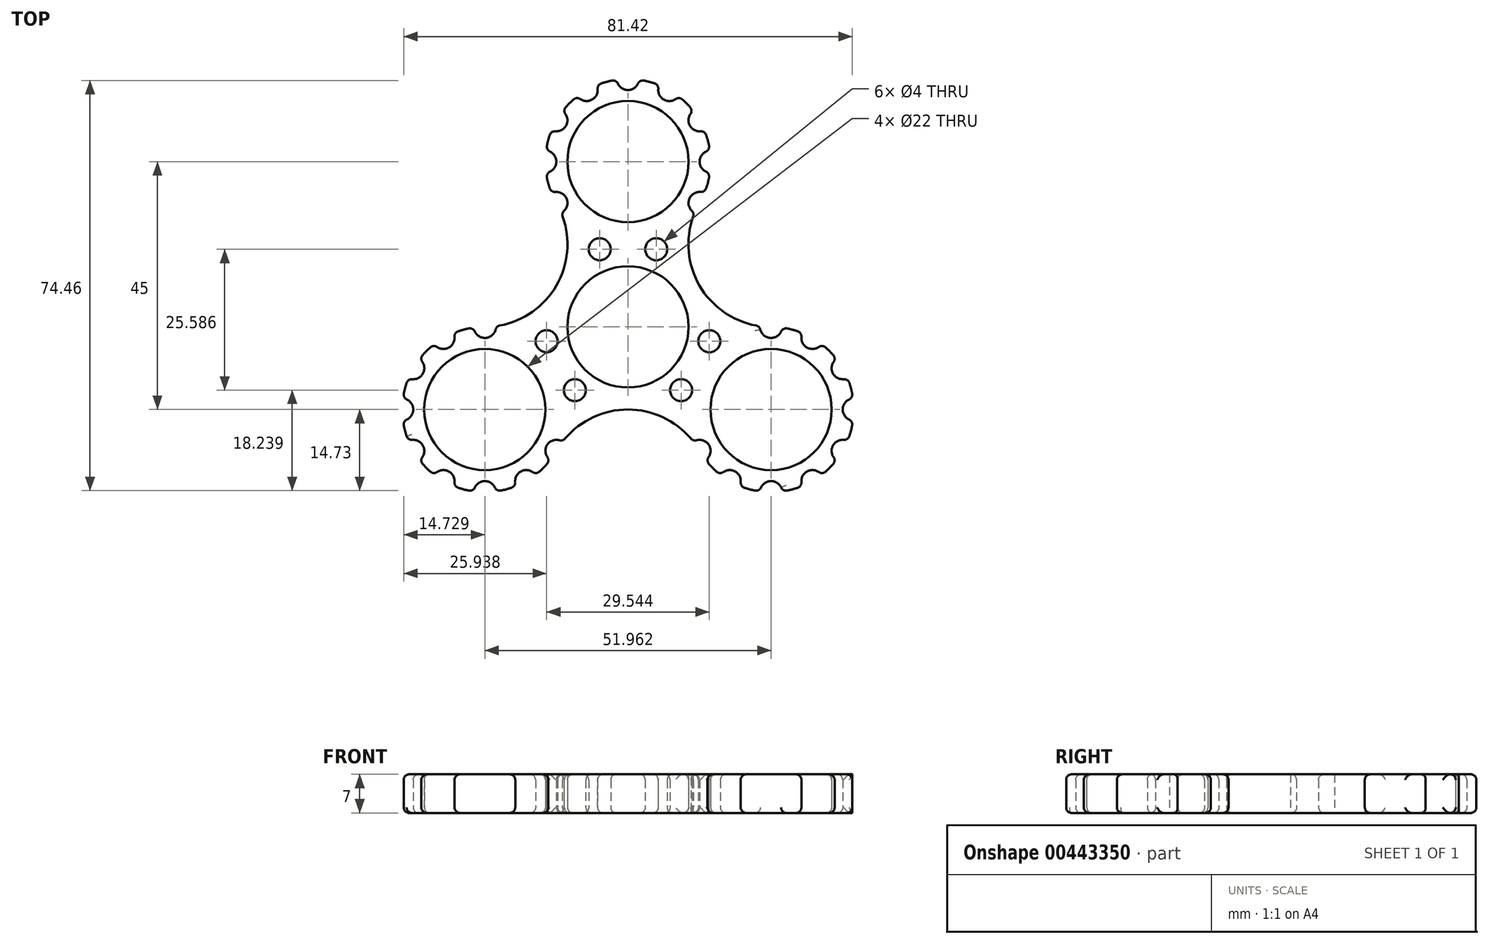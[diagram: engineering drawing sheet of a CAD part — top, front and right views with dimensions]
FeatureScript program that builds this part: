
annotation { "Feature Type Name" : "Feature", "Feature Type Description" : "" }
export const myFeature = defineFeature(function(context is Context, id is Id, definition is map)
    precondition{}
    {
        {
            var Q0;
            Q0=qCreatedBy(makeId("Top.planeOp"),FACE);
            var sketch = newSketch(context, id + "F0", { "sketchPlane" : qUnion([Q0])});
            skCircle(sketch, "E0", {"center": v(0, 0) * mm, "radius": 11 * mm});
            skCircle(sketch, "E1.0", {"center": v(0, 0) * mm, "radius": 14 * mm});
            skCircle(sketch, "E2", {"center": v(0, 30) * mm, "radius": 11 * mm});
            skArc(sketch, "E3.0", {"start": v(13, 22.5) * mm, "mid": v(0, 45) * mm, "end": v(-13, 22.5) * mm});
            skLineSegment(sketch, "E4", {"start": v(0, 14) * mm, "end": v(0, 30) * mm});
            skCircle(sketch, "E5.1.0", {"center": v(-25.98, -15) * mm, "radius": 11 * mm});
            skArc(sketch, "E5.1.1", {"start": v(-25.98, 0) * mm, "mid": v(-38.97, -22.5) * mm, "end": v(-13, -22.5) * mm});
            skCircle(sketch, "E5.2.0", {"center": v(25.98, -15) * mm, "radius": 11 * mm});
            skArc(sketch, "E5.2.1", {"start": v(13, -22.5) * mm, "mid": v(38.97, -22.5) * mm, "end": v(25.98, 0) * mm});
            skArc(sketch, "E6", {"start": v(-13, 22.5) * mm, "mid": v(-13, 7.5) * mm, "end": v(-25.98, 0) * mm});
            skArc(sketch, "E7", {"start": v(25.98, 0) * mm, "mid": v(13, 7.5) * mm, "end": v(13, 22.5) * mm});
            skArc(sketch, "E8", {"start": v(-13, -22.5) * mm, "mid": v(0, -15) * mm, "end": v(13, -22.5) * mm});
            skPoint(sketch, "E9", {"position": v(-13, 7.5) * mm});
            skCircle(sketch, "E10.1.0", {"center": v(-14.77, -2.6) * mm, "radius": 2 * mm});
            skCircle(sketch, "E10.2.0", {"center": v(-9.64, -11.5) * mm, "radius": 2 * mm});
            skCircle(sketch, "E10.4.0", {"center": v(9.64, -11.5) * mm, "radius": 2 * mm});
            skCircle(sketch, "E10.5.0", {"center": v(14.77, -2.6) * mm, "radius": 2 * mm});
            skCircle(sketch, "E10.7.0", {"center": v(5.13, 14.1) * mm, "radius": 2 * mm});
            skCircle(sketch, "E10.8.0", {"center": v(-5.13, 14.1) * mm, "radius": 2 * mm});
            skCircle(sketch, "E11", {"center": v(25.98, 0) * mm, "radius": 2 * mm});
            skCircle(sketch, "E12.1.0", {"center": v(33.48, -2) * mm, "radius": 2 * mm});
            skCircle(sketch, "E12.2.0", {"center": v(38.97, -7.5) * mm, "radius": 2 * mm});
            skCircle(sketch, "E12.3.0", {"center": v(40.98, -15) * mm, "radius": 2 * mm});
            skCircle(sketch, "E12.4.0", {"center": v(38.97, -22.5) * mm, "radius": 2 * mm});
            skCircle(sketch, "E12.5.0", {"center": v(33.48, -28) * mm, "radius": 2 * mm});
            skCircle(sketch, "E12.6.0", {"center": v(25.98, -30) * mm, "radius": 2 * mm});
            skCircle(sketch, "E12.7.0", {"center": v(18.48, -28) * mm, "radius": 2 * mm});
            skCircle(sketch, "E12.8.0", {"center": v(13, -22.5) * mm, "radius": 2 * mm});
            skLineSegment(sketch, "E12.anchor1", {"start": v(25.98, -15) * mm, "end": v(25.98, 0) * mm, "construction": true});
            skLineSegment(sketch, "E12.anchor2", {"start": v(25.98, -15) * mm, "end": v(13, -22.5) * mm, "construction": true});
            skCircle(sketch, "E13.1.0", {"center": v(-13, 22.5) * mm, "radius": 2 * mm});
            skCircle(sketch, "E13.1.1", {"center": v(-15, 30) * mm, "radius": 2 * mm});
            skCircle(sketch, "E13.1.2", {"center": v(-13, 37.5) * mm, "radius": 2 * mm});
            skCircle(sketch, "E13.1.3", {"center": v(-7.5, 43) * mm, "radius": 2 * mm});
            skCircle(sketch, "E13.1.4", {"center": v(0, 45) * mm, "radius": 2 * mm});
            skCircle(sketch, "E13.1.5", {"center": v(7.5, 43) * mm, "radius": 2 * mm});
            skCircle(sketch, "E13.1.6", {"center": v(13, 37.5) * mm, "radius": 2 * mm});
            skCircle(sketch, "E13.1.7", {"center": v(15, 30) * mm, "radius": 2 * mm});
            skCircle(sketch, "E13.1.8", {"center": v(13, 22.5) * mm, "radius": 2 * mm});
            skCircle(sketch, "E13.2.0", {"center": v(-13, -22.5) * mm, "radius": 2 * mm});
            skCircle(sketch, "E13.2.1", {"center": v(-18.48, -28) * mm, "radius": 2 * mm});
            skCircle(sketch, "E13.2.2", {"center": v(-25.98, -30) * mm, "radius": 2 * mm});
            skCircle(sketch, "E13.2.3", {"center": v(-33.48, -28) * mm, "radius": 2 * mm});
            skCircle(sketch, "E13.2.4", {"center": v(-38.97, -22.5) * mm, "radius": 2 * mm});
            skCircle(sketch, "E13.2.5", {"center": v(-40.98, -15) * mm, "radius": 2 * mm});
            skCircle(sketch, "E13.2.6", {"center": v(-38.97, -7.5) * mm, "radius": 2 * mm});
            skCircle(sketch, "E13.2.7", {"center": v(-33.48, -2) * mm, "radius": 2 * mm});
            skCircle(sketch, "E13.2.8", {"center": v(-25.98, 0) * mm, "radius": 2 * mm});
            skSolve(sketch);
        }
        {
            var Q0;
            Q0=makeQuery(id+"F0.imprint","IMPRINT",FACE,{"disambiguationData":[TD([[makeQuery(id+"F0.imprint","IMPRINT",EDGE,{"derivedFrom":sQuery(id+"F0.wireOp",EDGE,"E2")}),-1.0]])]});
            var Q1;
            Q1=makeQuery(id+"F0.imprint","IMPRINT",FACE,{"disambiguationData":[TD([[makeQuery(id+"F0.imprint","IMPRINT",EDGE,{"derivedFrom":sQuery(id+"F0.wireOp",EDGE,"E0")}),-1.0]])]});
            extrude(context, id + "F1", {"entities" : qUnion([Q0, Q1]), "endBound" : BoundingType.SYMMETRIC, "depth" : 7 * mm});
        }
        {
            var Q0;
            {var subQ0=sQuery(id+"F0.wireOp",EDGE,"E5.1.1");Q0=makeQuery(id+"F1.opExtrude","SWEPT_FACE",FACE,{"disambiguationData":[OSD([subQ0]),TDD([makeQuery(id+"F0.imprint","IMPRINT",EDGE,{"disambiguationData":[TD([[makeQuery(id+"F0.imprint","INTERSECT",VERTEX,{"disambiguationData":[OD(1.0)],"derivedFrom":[subQ0,sQuery(id+"F0.wireOp",EDGE,"E13.2.6")]}),-1.0]])],"derivedFrom":subQ0})])]});}
            var Q1;
            Q1=makeQuery(id+"F1.opExtrude","SWEPT_FACE",FACE,{"disambiguationData":[OSD([sQuery(id+"F0.wireOp",EDGE,"E13.2.5")])]});
            var Q2;
            {var subQ0=sQuery(id+"F0.wireOp",EDGE,"E5.1.1");Q2=makeQuery(id+"F1.opExtrude","SWEPT_FACE",FACE,{"disambiguationData":[OSD([subQ0]),TDD([makeQuery(id+"F0.imprint","IMPRINT",EDGE,{"disambiguationData":[TD([[makeQuery(id+"F0.imprint","INTERSECT",VERTEX,{"disambiguationData":[OD(1.0)],"derivedFrom":[subQ0,sQuery(id+"F0.wireOp",EDGE,"E13.2.5")]}),-1.0]])],"derivedFrom":subQ0})])]});}
            var Q3;
            Q3=makeQuery(id+"F1.opExtrude","SWEPT_FACE",FACE,{"disambiguationData":[OSD([sQuery(id+"F0.wireOp",EDGE,"E13.2.4")])]});
            var Q4;
            {var subQ0=sQuery(id+"F0.wireOp",EDGE,"E5.1.1");Q4=makeQuery(id+"F1.opExtrude","SWEPT_FACE",FACE,{"disambiguationData":[OSD([subQ0]),TDD([makeQuery(id+"F0.imprint","IMPRINT",EDGE,{"disambiguationData":[TD([[makeQuery(id+"F0.imprint","INTERSECT",VERTEX,{"disambiguationData":[OD(1.0)],"derivedFrom":[subQ0,sQuery(id+"F0.wireOp",EDGE,"E13.2.4")]}),-1.0]])],"derivedFrom":subQ0})])]});}
            var Q5;
            Q5=makeQuery(id+"F1.opExtrude","SWEPT_FACE",FACE,{"disambiguationData":[OSD([sQuery(id+"F0.wireOp",EDGE,"E13.2.3")])]});
            var Q6;
            {var subQ0=sQuery(id+"F0.wireOp",EDGE,"E5.1.1");Q6=makeQuery(id+"F1.opExtrude","SWEPT_FACE",FACE,{"disambiguationData":[OSD([subQ0]),TDD([makeQuery(id+"F0.imprint","IMPRINT",EDGE,{"disambiguationData":[TD([[makeQuery(id+"F0.imprint","INTERSECT",VERTEX,{"disambiguationData":[OD(1.0)],"derivedFrom":[subQ0,sQuery(id+"F0.wireOp",EDGE,"E13.2.3")]}),-1.0]])],"derivedFrom":subQ0})])]});}
            var Q7;
            Q7=makeQuery(id+"F1.opExtrude","SWEPT_FACE",FACE,{"disambiguationData":[OSD([sQuery(id+"F0.wireOp",EDGE,"E13.2.2")])]});
            var Q8;
            {var subQ0=sQuery(id+"F0.wireOp",EDGE,"E5.1.1");Q8=makeQuery(id+"F1.opExtrude","SWEPT_FACE",FACE,{"disambiguationData":[OSD([subQ0]),TDD([makeQuery(id+"F0.imprint","IMPRINT",EDGE,{"disambiguationData":[TD([[makeQuery(id+"F0.imprint","INTERSECT",VERTEX,{"disambiguationData":[OD(1.0)],"derivedFrom":[subQ0,sQuery(id+"F0.wireOp",EDGE,"E13.2.2")]}),-1.0]])],"derivedFrom":subQ0})])]});}
            var Q9;
            Q9=makeQuery(id+"F1.opExtrude","SWEPT_FACE",FACE,{"disambiguationData":[OSD([sQuery(id+"F0.wireOp",EDGE,"E13.2.6")])]});
            var Q10;
            Q10=makeQuery(id+"F1.opExtrude","SWEPT_FACE",FACE,{"disambiguationData":[OSD([sQuery(id+"F0.wireOp",EDGE,"E13.2.1")])]});
            var Q11;
            {var subQ0=sQuery(id+"F0.wireOp",EDGE,"E5.1.1");Q11=makeQuery(id+"F1.opExtrude","SWEPT_FACE",FACE,{"disambiguationData":[OSD([subQ0]),TDD([makeQuery(id+"F0.imprint","IMPRINT",EDGE,{"disambiguationData":[TD([[makeQuery(id+"F0.imprint","INTERSECT",VERTEX,{"disambiguationData":[OD(1.0)],"derivedFrom":[subQ0,sQuery(id+"F0.wireOp",EDGE,"E13.2.1")]}),-1.0]])],"derivedFrom":subQ0})])]});}
            var Q12;
            Q12=makeQuery(id+"F1.opExtrude","SWEPT_FACE",FACE,{"disambiguationData":[OSD([sQuery(id+"F0.wireOp",EDGE,"E13.2.0")])]});
            var Q13;
            Q13=makeQuery(id+"F1.opExtrude","SWEPT_FACE",FACE,{"disambiguationData":[OSD([sQuery(id+"F0.wireOp",EDGE,"E8")])]});
            var Q14;
            Q14=makeQuery(id+"F1.opExtrude","SWEPT_FACE",FACE,{"disambiguationData":[OSD([sQuery(id+"F0.wireOp",EDGE,"E12.8.0")])]});
            var Q15;
            {var subQ0=sQuery(id+"F0.wireOp",EDGE,"E5.2.1");Q15=makeQuery(id+"F1.opExtrude","SWEPT_FACE",FACE,{"disambiguationData":[OSD([subQ0]),TDD([makeQuery(id+"F0.imprint","IMPRINT",EDGE,{"disambiguationData":[TD([[makeQuery(id+"F0.imprint","INTERSECT",VERTEX,{"derivedFrom":[subQ0,sQuery(id+"F0.wireOp",EDGE,"E12.8.0")]}),-1.0]])],"derivedFrom":subQ0})])]});}
            var Q16;
            Q16=makeQuery(id+"F1.opExtrude","SWEPT_FACE",FACE,{"disambiguationData":[OSD([sQuery(id+"F0.wireOp",EDGE,"E12.7.0")])]});
            var Q17;
            {var subQ0=sQuery(id+"F0.wireOp",EDGE,"E5.2.1");Q17=makeQuery(id+"F1.opExtrude","SWEPT_FACE",FACE,{"disambiguationData":[OSD([subQ0]),TDD([makeQuery(id+"F0.imprint","IMPRINT",EDGE,{"disambiguationData":[TD([[makeQuery(id+"F0.imprint","INTERSECT",VERTEX,{"disambiguationData":[OD(1.0)],"derivedFrom":[subQ0,sQuery(id+"F0.wireOp",EDGE,"E12.7.0")]}),-1.0]])],"derivedFrom":subQ0})])]});}
            var Q18;
            Q18=makeQuery(id+"F1.opExtrude","SWEPT_FACE",FACE,{"disambiguationData":[OSD([sQuery(id+"F0.wireOp",EDGE,"E12.6.0")])]});
            var Q19;
            {var subQ0=sQuery(id+"F0.wireOp",EDGE,"E5.2.1");Q19=makeQuery(id+"F1.opExtrude","SWEPT_FACE",FACE,{"disambiguationData":[OSD([subQ0]),TDD([makeQuery(id+"F0.imprint","IMPRINT",EDGE,{"disambiguationData":[TD([[makeQuery(id+"F0.imprint","INTERSECT",VERTEX,{"disambiguationData":[OD(1.0)],"derivedFrom":[subQ0,sQuery(id+"F0.wireOp",EDGE,"E12.6.0")]}),-1.0]])],"derivedFrom":subQ0})])]});}
            var Q20;
            Q20=makeQuery(id+"F1.opExtrude","SWEPT_FACE",FACE,{"disambiguationData":[OSD([sQuery(id+"F0.wireOp",EDGE,"E12.5.0")])]});
            var Q21;
            {var subQ0=sQuery(id+"F0.wireOp",EDGE,"E5.2.1");Q21=makeQuery(id+"F1.opExtrude","SWEPT_FACE",FACE,{"disambiguationData":[OSD([subQ0]),TDD([makeQuery(id+"F0.imprint","IMPRINT",EDGE,{"disambiguationData":[TD([[makeQuery(id+"F0.imprint","INTERSECT",VERTEX,{"disambiguationData":[OD(1.0)],"derivedFrom":[subQ0,sQuery(id+"F0.wireOp",EDGE,"E12.5.0")]}),-1.0]])],"derivedFrom":subQ0})])]});}
            var Q22;
            Q22=makeQuery(id+"F1.opExtrude","SWEPT_FACE",FACE,{"disambiguationData":[OSD([sQuery(id+"F0.wireOp",EDGE,"E12.4.0")])]});
            var Q23;
            {var subQ0=sQuery(id+"F0.wireOp",EDGE,"E5.2.1");Q23=makeQuery(id+"F1.opExtrude","SWEPT_FACE",FACE,{"disambiguationData":[OSD([subQ0]),TDD([makeQuery(id+"F0.imprint","IMPRINT",EDGE,{"disambiguationData":[TD([[makeQuery(id+"F0.imprint","INTERSECT",VERTEX,{"disambiguationData":[OD(1.0)],"derivedFrom":[subQ0,sQuery(id+"F0.wireOp",EDGE,"E12.4.0")]}),-1.0]])],"derivedFrom":subQ0})])]});}
            var Q24;
            Q24=makeQuery(id+"F1.opExtrude","SWEPT_FACE",FACE,{"disambiguationData":[OSD([sQuery(id+"F0.wireOp",EDGE,"E12.3.0")])]});
            var Q25;
            {var subQ0=sQuery(id+"F0.wireOp",EDGE,"E5.2.1");Q25=makeQuery(id+"F1.opExtrude","SWEPT_FACE",FACE,{"disambiguationData":[OSD([subQ0]),TDD([makeQuery(id+"F0.imprint","IMPRINT",EDGE,{"disambiguationData":[TD([[makeQuery(id+"F0.imprint","INTERSECT",VERTEX,{"disambiguationData":[OD(1.0)],"derivedFrom":[subQ0,sQuery(id+"F0.wireOp",EDGE,"E12.3.0")]}),-1.0]])],"derivedFrom":subQ0})])]});}
            var Q26;
            {var subQ0=sQuery(id+"F0.wireOp",EDGE,"E5.2.1");Q26=makeQuery(id+"F1.opExtrude","SWEPT_FACE",FACE,{"disambiguationData":[OSD([subQ0]),TDD([makeQuery(id+"F0.imprint","IMPRINT",EDGE,{"disambiguationData":[TD([[makeQuery(id+"F0.imprint","INTERSECT",VERTEX,{"disambiguationData":[OD(1.0)],"derivedFrom":[subQ0,sQuery(id+"F0.wireOp",EDGE,"E12.2.0")]}),-1.0]])],"derivedFrom":subQ0})])]});}
            var Q27;
            Q27=makeQuery(id+"F1.opExtrude","SWEPT_FACE",FACE,{"disambiguationData":[OSD([sQuery(id+"F0.wireOp",EDGE,"E12.1.0")])]});
            var Q28;
            Q28=makeQuery(id+"F1.opExtrude","SWEPT_FACE",FACE,{"disambiguationData":[OSD([sQuery(id+"F0.wireOp",EDGE,"E12.2.0")])]});
            var Q29;
            {var subQ0=sQuery(id+"F0.wireOp",EDGE,"E5.2.1");Q29=makeQuery(id+"F1.opExtrude","SWEPT_FACE",FACE,{"disambiguationData":[OSD([subQ0]),TDD([makeQuery(id+"F0.imprint","IMPRINT",EDGE,{"disambiguationData":[TD([[makeQuery(id+"F0.imprint","INTERSECT",VERTEX,{"disambiguationData":[OD(1.0)],"derivedFrom":[subQ0,sQuery(id+"F0.wireOp",EDGE,"E12.1.0")]}),-1.0]])],"derivedFrom":subQ0})])]});}
            var Q30;
            Q30=makeQuery(id+"F1.opExtrude","SWEPT_FACE",FACE,{"disambiguationData":[OSD([sQuery(id+"F0.wireOp",EDGE,"E11")])]});
            var Q31;
            Q31=makeQuery(id+"F1.opExtrude","SWEPT_FACE",FACE,{"disambiguationData":[OSD([sQuery(id+"F0.wireOp",EDGE,"E7")])]});
            var Q32;
            Q32=makeQuery(id+"F1.opExtrude","SWEPT_FACE",FACE,{"disambiguationData":[OSD([sQuery(id+"F0.wireOp",EDGE,"E10.7.0")])]});
            var Q33;
            Q33=makeQuery(id+"F1.opExtrude","SWEPT_FACE",FACE,{"disambiguationData":[OSD([sQuery(id+"F0.wireOp",EDGE,"E13.1.8")])]});
            var Q34;
            {var subQ0=sQuery(id+"F0.wireOp",EDGE,"E3.0");Q34=makeQuery(id+"F1.opExtrude","SWEPT_FACE",FACE,{"disambiguationData":[OSD([subQ0]),TDD([makeQuery(id+"F0.imprint","IMPRINT",EDGE,{"disambiguationData":[TD([[makeQuery(id+"F0.imprint","INTERSECT",VERTEX,{"derivedFrom":[subQ0,sQuery(id+"F0.wireOp",EDGE,"E13.1.8")]}),-1.0]])],"derivedFrom":subQ0})])]});}
            var Q35;
            {var subQ0=sQuery(id+"F0.wireOp",EDGE,"E3.0");Q35=makeQuery(id+"F1.opExtrude","SWEPT_FACE",FACE,{"disambiguationData":[OSD([subQ0]),TDD([makeQuery(id+"F0.imprint","IMPRINT",EDGE,{"disambiguationData":[TD([[makeQuery(id+"F0.imprint","INTERSECT",VERTEX,{"disambiguationData":[OD(1.0)],"derivedFrom":[subQ0,sQuery(id+"F0.wireOp",EDGE,"E13.1.7")]}),-1.0]])],"derivedFrom":subQ0})])]});}
            var Q36;
            Q36=makeQuery(id+"F1.opExtrude","SWEPT_FACE",FACE,{"disambiguationData":[OSD([sQuery(id+"F0.wireOp",EDGE,"E13.1.6")])]});
            var Q37;
            Q37=makeQuery(id+"F1.opExtrude","SWEPT_FACE",FACE,{"disambiguationData":[OSD([sQuery(id+"F0.wireOp",EDGE,"E13.1.7")])]});
            var Q38;
            Q38=makeQuery(id+"F1.opExtrude","SWEPT_FACE",FACE,{"disambiguationData":[OSD([sQuery(id+"F0.wireOp",EDGE,"E13.1.5")])]});
            var Q39;
            {var subQ0=sQuery(id+"F0.wireOp",EDGE,"E3.0");Q39=makeQuery(id+"F1.opExtrude","SWEPT_FACE",FACE,{"disambiguationData":[OSD([subQ0]),TDD([makeQuery(id+"F0.imprint","IMPRINT",EDGE,{"disambiguationData":[TD([[makeQuery(id+"F0.imprint","INTERSECT",VERTEX,{"disambiguationData":[OD(1.0)],"derivedFrom":[subQ0,sQuery(id+"F0.wireOp",EDGE,"E13.1.5")]}),-1.0]])],"derivedFrom":subQ0})])]});}
            var Q40;
            Q40=makeQuery(id+"F1.opExtrude","SWEPT_FACE",FACE,{"disambiguationData":[OSD([sQuery(id+"F0.wireOp",EDGE,"E13.1.4")])]});
            var Q41;
            {var subQ0=sQuery(id+"F0.wireOp",EDGE,"E3.0");Q41=makeQuery(id+"F1.opExtrude","SWEPT_FACE",FACE,{"disambiguationData":[OSD([subQ0]),TDD([makeQuery(id+"F0.imprint","IMPRINT",EDGE,{"disambiguationData":[TD([[makeQuery(id+"F0.imprint","INTERSECT",VERTEX,{"disambiguationData":[OD(1.0)],"derivedFrom":[subQ0,sQuery(id+"F0.wireOp",EDGE,"E13.1.4")]}),-1.0]])],"derivedFrom":subQ0})])]});}
            var Q42;
            Q42=makeQuery(id+"F1.opExtrude","SWEPT_FACE",FACE,{"disambiguationData":[OSD([sQuery(id+"F0.wireOp",EDGE,"E13.1.3")])]});
            var Q43;
            {var subQ0=sQuery(id+"F0.wireOp",EDGE,"E3.0");Q43=makeQuery(id+"F1.opExtrude","SWEPT_FACE",FACE,{"disambiguationData":[OSD([subQ0]),TDD([makeQuery(id+"F0.imprint","IMPRINT",EDGE,{"disambiguationData":[TD([[makeQuery(id+"F0.imprint","INTERSECT",VERTEX,{"disambiguationData":[OD(1.0)],"derivedFrom":[subQ0,sQuery(id+"F0.wireOp",EDGE,"E13.1.3")]}),-1.0]])],"derivedFrom":subQ0})])]});}
            var Q44;
            Q44=makeQuery(id+"F1.opExtrude","SWEPT_FACE",FACE,{"disambiguationData":[OSD([sQuery(id+"F0.wireOp",EDGE,"E13.1.2")])]});
            var Q45;
            {var subQ0=sQuery(id+"F0.wireOp",EDGE,"E3.0");Q45=makeQuery(id+"F1.opExtrude","SWEPT_FACE",FACE,{"disambiguationData":[OSD([subQ0]),TDD([makeQuery(id+"F0.imprint","IMPRINT",EDGE,{"disambiguationData":[TD([[makeQuery(id+"F0.imprint","INTERSECT",VERTEX,{"disambiguationData":[OD(1.0)],"derivedFrom":[subQ0,sQuery(id+"F0.wireOp",EDGE,"E13.1.2")]}),-1.0]])],"derivedFrom":subQ0})])]});}
            var Q46;
            Q46=makeQuery(id+"F1.opExtrude","SWEPT_FACE",FACE,{"disambiguationData":[OSD([sQuery(id+"F0.wireOp",EDGE,"E13.1.1")])]});
            var Q47;
            Q47=makeQuery(id+"F1.opExtrude","SWEPT_EDGE",EDGE,{"disambiguationData":[OSD([sQuery(id+"F0.wireOp",EDGE,"E3.0"),sQuery(id+"F0.wireOp",EDGE,"E13.1.0")])]});
            var Q48;
            Q48=makeQuery(id+"F1.opExtrude","SWEPT_FACE",FACE,{"disambiguationData":[OSD([sQuery(id+"F0.wireOp",EDGE,"E13.1.0")])]});
            var Q49;
            Q49=makeQuery(id+"F1.opExtrude","SWEPT_FACE",FACE,{"disambiguationData":[OSD([sQuery(id+"F0.wireOp",EDGE,"E6")])]});
            var Q50;
            Q50=makeQuery(id+"F1.opExtrude","SWEPT_FACE",FACE,{"disambiguationData":[OSD([sQuery(id+"F0.wireOp",EDGE,"E13.2.8")])]});
            var Q51;
            {var subQ0=sQuery(id+"F0.wireOp",EDGE,"E5.1.1");Q51=makeQuery(id+"F1.opExtrude","SWEPT_FACE",FACE,{"disambiguationData":[OSD([subQ0]),TDD([makeQuery(id+"F0.imprint","IMPRINT",EDGE,{"disambiguationData":[TD([[makeQuery(id+"F0.imprint","INTERSECT",VERTEX,{"derivedFrom":[subQ0,sQuery(id+"F0.wireOp",EDGE,"E13.2.8")]}),-1.0]])],"derivedFrom":subQ0})])]});}
            var Q52;
            Q52=makeQuery(id+"F1.opExtrude","SWEPT_FACE",FACE,{"disambiguationData":[OSD([sQuery(id+"F0.wireOp",EDGE,"E13.2.7")])]});
            var Q53;
            {var subQ0=sQuery(id+"F0.wireOp",EDGE,"E5.1.1");Q53=makeQuery(id+"F1.opExtrude","SWEPT_FACE",FACE,{"disambiguationData":[OSD([subQ0]),TDD([makeQuery(id+"F0.imprint","IMPRINT",EDGE,{"disambiguationData":[TD([[makeQuery(id+"F0.imprint","INTERSECT",VERTEX,{"disambiguationData":[OD(1.0)],"derivedFrom":[subQ0,sQuery(id+"F0.wireOp",EDGE,"E13.2.7")]}),-1.0]])],"derivedFrom":subQ0})])]});}
            var Q54;
            Q54=makeQuery(id+"F1.opExtrude","SWEPT_FACE",FACE,{"disambiguationData":[OSD([sQuery(id+"F0.wireOp",EDGE,"E10.1.0")])]});
            var Q55;
            Q55=makeQuery(id+"F1.opExtrude","SWEPT_FACE",FACE,{"disambiguationData":[OSD([sQuery(id+"F0.wireOp",EDGE,"E10.2.0")])]});
            var Q56;
            Q56=makeQuery(id+"F1.opExtrude","SWEPT_FACE",FACE,{"disambiguationData":[OSD([sQuery(id+"F0.wireOp",EDGE,"E10.4.0")])]});
            var Q57;
            Q57=makeQuery(id+"F1.opExtrude","SWEPT_FACE",FACE,{"disambiguationData":[OSD([sQuery(id+"F0.wireOp",EDGE,"E10.5.0")])]});
            var Q58;
            Q58=makeQuery(id+"F1.opExtrude","SWEPT_FACE",FACE,{"disambiguationData":[OSD([sQuery(id+"F0.wireOp",EDGE,"E10.8.0")])]});
            fillet(context, id + "F2", {"entities" : qUnion([Q0, Q1, Q2, Q3, Q4, Q5, Q6, Q7, Q8, Q9, Q10, Q11, Q12, Q13, Q14, Q15, Q16, Q17, Q18, Q19, Q20, Q21, Q22, Q23, Q24, Q25, Q26, Q27, Q28, Q29, Q30, Q31, Q32, Q33, Q34, Q35, Q36, Q37, Q38, Q39, Q40, Q41, Q42, Q43, Q44, Q45, Q46, Q47, Q48, Q49, Q50, Q51, Q52, Q53, Q54, Q55, Q56, Q57, Q58]), "radius" : 1 * mm, "tangentPropagation" : true, "allowEdgeOverflow" : false});
        }
    });
